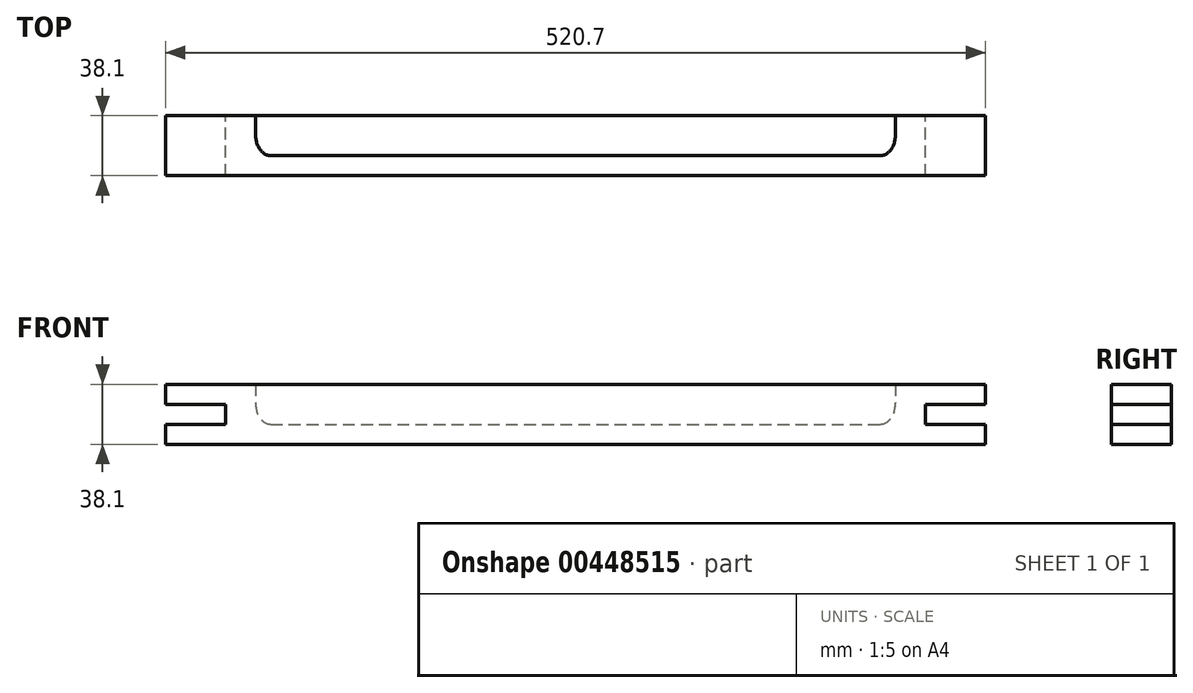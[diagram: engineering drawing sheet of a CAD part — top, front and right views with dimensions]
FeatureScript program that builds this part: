
annotation { "Feature Type Name" : "Feature", "Feature Type Description" : "" }
export const myFeature = defineFeature(function(context is Context, id is Id, definition is map)
    precondition{}
    {
        {
            var Q0;
            Q0=qCreatedBy(makeId("Front.planeOp"),FACE);
            var sketch = newSketch(context, id + "F0", { "sketchPlane" : qUnion([Q0])});
            skLineSegment(sketch, "E0.bottom", {"start": v(0, 0) * mm, "end": v(520.7, 0) * mm});
            skLineSegment(sketch, "E0.top", {"start": v(0, -38.1) * mm, "end": v(520.7, -38.1) * mm});
            skLineSegment(sketch, "E0.left", {"start": v(0, 0) * mm, "end": v(0, -12.7) * mm});
            skLineSegment(sketch, "E0.right", {"start": v(520.7, 0) * mm, "end": v(520.7, -12.7) * mm});
            skLineSegment(sketch, "E1", {"start": v(0, -12.7) * mm, "end": v(38.1, -12.7) * mm});
            skLineSegment(sketch, "E2", {"start": v(38.1, -12.7) * mm, "end": v(38.1, -25.4) * mm});
            skLineSegment(sketch, "E3", {"start": v(38.1, -25.4) * mm, "end": v(0, -25.4) * mm});
            skLineSegment(sketch, "E4.trimOffspring", {"start": v(0, -25.4) * mm, "end": v(0, -38.1) * mm});
            skLineSegment(sketch, "E5.bottom", {"start": v(520.7, -12.7) * mm, "end": v(482.6, -12.7) * mm});
            skLineSegment(sketch, "E5.top", {"start": v(520.7, -25.4) * mm, "end": v(482.6, -25.4) * mm});
            skLineSegment(sketch, "E5.right", {"start": v(482.6, -12.7) * mm, "end": v(482.6, -25.4) * mm});
            skLineSegment(sketch, "E6.trimOffspring", {"start": v(520.7, -25.4) * mm, "end": v(520.7, -38.1) * mm});
            skSolve(sketch);
        }
        {
            var Q0;
            Q0=makeQuery(id+"F0.imprint","IMPRINT",FACE,{"disambiguationData":[TD([[makeQuery(id+"F0.imprint","IMPRINT",EDGE,{"derivedFrom":sQuery(id+"F0.wireOp",EDGE,"E0.bottom")}),-1.0]])]});
            extrude(context, id + "F1", {"entities" : qUnion([Q0]), "depth" : 38.1 * mm});
        }
        {
            var Q0;
            Q0=makeQuery(id+"F1.opExtrude","SWEPT_FACE",FACE,{"disambiguationData":[OSD([sQuery(id+"F0.wireOp",EDGE,"E0.right")])]});
            cPlane(context, id + "F2", {"entities" : qUnion([Q0]), "cplaneType" : CPlaneType.OFFSET, "offset" : 260.35 * mm, "oppositeDirection" : true, "width" : 152.4 * mm, "height" : 152.4 * mm});
        }
        {
            var Q0;
            Q0=qCreatedBy(id+"F2.planeOp",FACE);
            var sketch = newSketch(context, id + "F3", { "sketchPlane" : qUnion([Q0])});
            skLineSegment(sketch, "E7", {"start": v(0, 0) * mm, "end": v(0, -25.4) * mm});
            skLineSegment(sketch, "E8", {"start": v(0, 0) * mm, "end": v(-25.4, 0) * mm});
            skLineSegment(sketch, "E9", {"start": v(-25.4, 0) * mm, "end": v(0, -25.4) * mm});
            skSolve(sketch);
        }
        {
            var Q0;
            Q0 = qSketchRegion(id + "F3", true);
            extrude(context, id + "F4", {"entities" : qUnion([Q0]), "operationType" : NewBodyOperationType.REMOVE, "endBound" : BoundingType.SYMMETRIC, "oppositeDirection" : true, "depth" : 406.4 * mm, "offsetDistance" : 25.4 * mm});
        }
        {
            var Q0;
            Q0=makeQuery(id+"F4.boolean.opBoolean","COPY",EDGE,{"derivedFrom":makeQuery(id+"F4.opExtrude","CAP_EDGE",EDGE,{"disambiguationData":[OSD([sQuery(id+"F3.wireOp",EDGE,"E9")])],"isStart":true})});
            var Q1;
            Q1=makeQuery(id+"F4.boolean.opBoolean","COPY",EDGE,{"derivedFrom":makeQuery(id+"F4.opExtrude","CAP_EDGE",EDGE,{"disambiguationData":[OSD([sQuery(id+"F3.wireOp",EDGE,"E9")])],"isStart":false})});
            fillet(context, id + "F5", {"entities" : qUnion([Q0, Q1]), "radius" : 9.52 * mm, "tangentPropagation" : true, "allowEdgeOverflow" : false});
        }
    });
